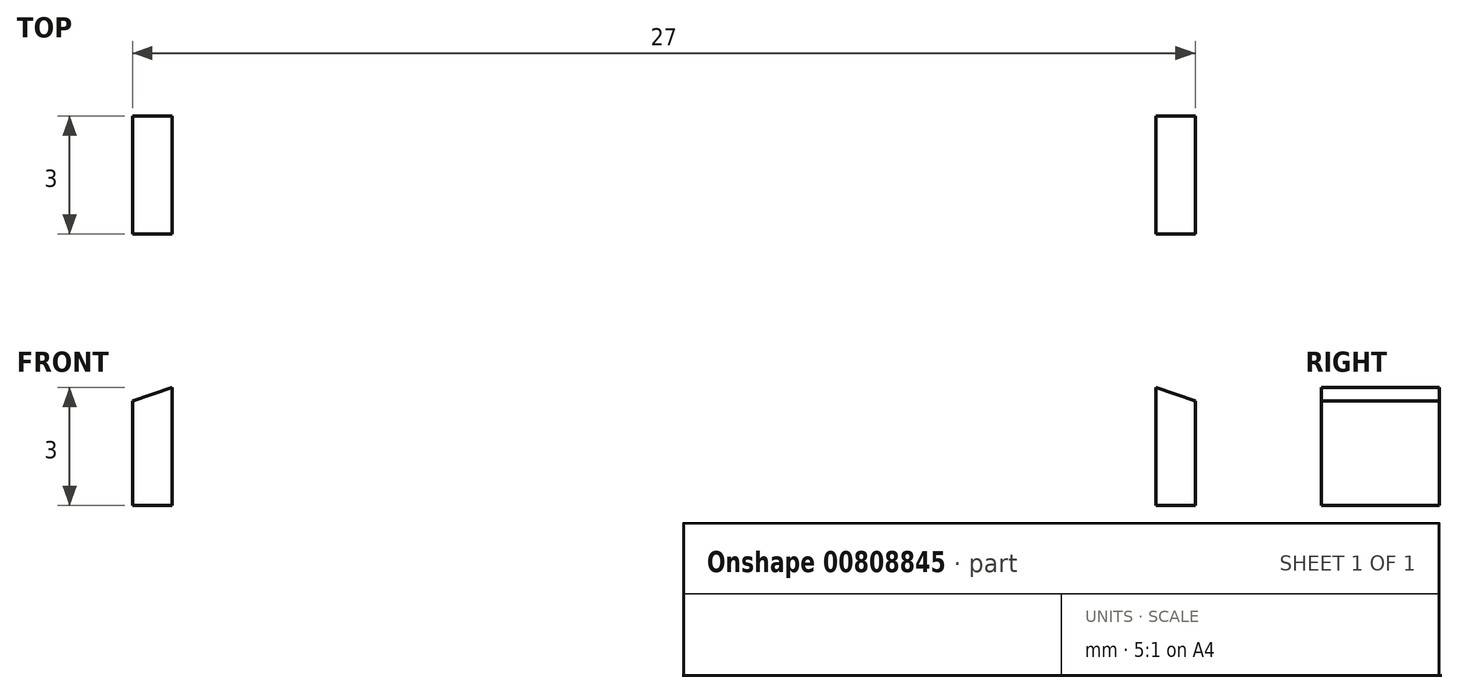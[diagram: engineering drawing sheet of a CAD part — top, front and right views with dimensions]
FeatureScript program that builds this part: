
annotation { "Feature Type Name" : "Feature", "Feature Type Description" : "" }
export const myFeature = defineFeature(function(context is Context, id is Id, definition is map)
    precondition{}
    {
        {
            var Q0;
            Q0=qCreatedBy(makeId("Front.planeOp"),FACE);
            var sketch = newSketch(context, id + "F0", { "sketchPlane" : qUnion([Q0])});
            skLineSegment(sketch, "E0.bottom", {"start": v(-35.5, 39) * mm, "end": v(35.5, 39) * mm});
            skLineSegment(sketch, "E0.top", {"start": v(-35.5, -39) * mm, "end": v(35.5, -39) * mm});
            skLineSegment(sketch, "E0.left", {"start": v(-35.5, 39) * mm, "end": v(-35.5, -39) * mm});
            skLineSegment(sketch, "E0.right", {"start": v(35.5, 39) * mm, "end": v(35.5, -39) * mm});
            skPoint(sketch, "E0.middle", {"position": v(0, 0) * mm});
            skLineSegment(sketch, "E1.top", {"start": v(-35.5, 31) * mm, "end": v(35.5, 31) * mm});
            skLineSegment(sketch, "E1.left", {"start": v(-35.5, -39) * mm, "end": v(-35.5, 31) * mm});
            skLineSegment(sketch, "E1.right", {"start": v(35.5, -39) * mm, "end": v(35.5, 31) * mm});
            skLineSegment(sketch, "E2.bottom", {"start": v(-12.5, 39) * mm, "end": v(12.5, 39) * mm});
            skLineSegment(sketch, "E2.top", {"start": v(-12.5, 31) * mm, "end": v(12.5, 31) * mm});
            skLineSegment(sketch, "E2.left", {"start": v(-12.5, 39) * mm, "end": v(-12.5, 31) * mm});
            skLineSegment(sketch, "E2.right", {"start": v(12.5, 39) * mm, "end": v(12.5, 31) * mm});
            skLineSegment(sketch, "E3", {"start": v(-35.5, 31) * mm, "end": v(-12.5, 39) * mm});
            skLineSegment(sketch, "E4", {"start": v(12.5, 39) * mm, "end": v(35.5, 31) * mm});
            skLineSegment(sketch, "E5.bottom", {"start": v(-32.5, -10) * mm, "end": v(-38.5, -10) * mm});
            skLineSegment(sketch, "E5.top", {"start": v(-32.5, 10) * mm, "end": v(-38.5, 10) * mm});
            skLineSegment(sketch, "E5.left", {"start": v(-32.5, -10) * mm, "end": v(-32.5, 10) * mm});
            skLineSegment(sketch, "E5.right", {"start": v(-38.5, -10) * mm, "end": v(-38.5, 10) * mm});
            skPoint(sketch, "E5.middle", {"position": v(-35.5, 0) * mm});
            skLineSegment(sketch, "E6.bottom", {"start": v(32.5, -10) * mm, "end": v(38.5, -10) * mm});
            skLineSegment(sketch, "E6.top", {"start": v(32.5, 10) * mm, "end": v(38.5, 10) * mm});
            skLineSegment(sketch, "E6.left", {"start": v(32.5, -10) * mm, "end": v(32.5, 10) * mm});
            skLineSegment(sketch, "E6.right", {"start": v(38.5, -10) * mm, "end": v(38.5, 10) * mm});
            skPoint(sketch, "E6.middle", {"position": v(35.5, 0) * mm});
            skLineSegment(sketch, "E7.bottom", {"start": v(-10, -42) * mm, "end": v(10, -42) * mm});
            skLineSegment(sketch, "E7.top", {"start": v(-10, -36) * mm, "end": v(10, -36) * mm});
            skLineSegment(sketch, "E7.left", {"start": v(-10, -42) * mm, "end": v(-10, -36) * mm});
            skLineSegment(sketch, "E7.right", {"start": v(10, -42) * mm, "end": v(10, -36) * mm});
            skPoint(sketch, "E7.middle", {"position": v(0, -39) * mm});
            skLineSegment(sketch, "E8.bottom", {"start": v(-12.5, 39) * mm, "end": v(-13.5, 39) * mm});
            skLineSegment(sketch, "E8.top", {"start": v(-12.5, 36) * mm, "end": v(-13.5, 36) * mm});
            skLineSegment(sketch, "E8.left", {"start": v(-12.5, 39) * mm, "end": v(-12.5, 36) * mm});
            skLineSegment(sketch, "E8.right", {"start": v(-13.5, 39) * mm, "end": v(-13.5, 36) * mm});
            skLineSegment(sketch, "E9.bottom", {"start": v(12.5, 39) * mm, "end": v(13.5, 39) * mm});
            skLineSegment(sketch, "E9.top", {"start": v(12.5, 36) * mm, "end": v(13.5, 36) * mm});
            skLineSegment(sketch, "E9.left", {"start": v(12.5, 39) * mm, "end": v(12.5, 36) * mm});
            skLineSegment(sketch, "E9.right", {"start": v(13.5, 39) * mm, "end": v(13.5, 36) * mm});
            skSolve(sketch);
        }
        {
            var Q0;
            {var subQ0=sQuery(id+"F0.wireOp",EDGE,"E2.top");Q0=makeQuery(id+"F0.imprint","IMPRINT",FACE,{"disambiguationData":[TD([[makeQuery(id+"F0.imprint","IMPRINT",EDGE,{"derivedFrom":subQ0}),-1.0]])]});}
            var Q1;
            {var subQ6=sQuery(id+"F0.wireOp",EDGE,"E2.left");Q1=makeQuery(id+"F0.imprint","IMPRINT",FACE,{"disambiguationData":[TD([[makeQuery(id+"F0.imprint","IMPRINT",EDGE,{"derivedFrom":subQ6}),-1.0]])]});}
            var Q2;
            {var subQ6=sQuery(id+"F0.wireOp",EDGE,"E2.right");Q2=makeQuery(id+"F0.imprint","IMPRINT",FACE,{"disambiguationData":[TD([[makeQuery(id+"F0.imprint","IMPRINT",EDGE,{"derivedFrom":subQ6}),1.0]])]});}
            extrude(context, id + "F1", {"entities" : qUnion([Q0, Q1, Q2]), "depth" : 3 * mm, "offsetDistance" : 25 * mm});
        }
        {
            var Q0;
            Q0=makeQuery(id+"F1.opExtrude","CAP_FACE",FACE,{"disambiguationData":[OSD([sQuery(id+"F0.wireOp",EDGE,"E0.top"),sQuery(id+"F0.wireOp",EDGE,"E1.left"),sQuery(id+"F0.wireOp",EDGE,"E1.right"),sQuery(id+"F0.wireOp",EDGE,"E2.top"),sQuery(id+"F0.wireOp",EDGE,"E2.left"),sQuery(id+"F0.wireOp",EDGE,"E2.right"),sQuery(id+"F0.wireOp",EDGE,"E3"),sQuery(id+"F0.wireOp",EDGE,"E4"),sQuery(id+"F0.wireOp",EDGE,"E5.bottom"),sQuery(id+"F0.wireOp",EDGE,"E5.top"),sQuery(id+"F0.wireOp",EDGE,"E5.left"),sQuery(id+"F0.wireOp",EDGE,"E6.bottom"),sQuery(id+"F0.wireOp",EDGE,"E6.top"),sQuery(id+"F0.wireOp",EDGE,"E6.left"),sQuery(id+"F0.wireOp",EDGE,"E7.top"),sQuery(id+"F0.wireOp",EDGE,"E7.left"),sQuery(id+"F0.wireOp",EDGE,"E7.right"),sQuery(id+"F0.wireOp",EDGE,"E8.top"),sQuery(id+"F0.wireOp",EDGE,"E8.right"),sQuery(id+"F0.wireOp",EDGE,"E9.top"),sQuery(id+"F0.wireOp",EDGE,"E9.right")])],"isStart":false});
            var sketch = newSketch(context, id + "F2", { "sketchPlane" : qUnion([Q0])});
            skLineSegment(sketch, "E10.bottom", {"start": v(22.5, 31) * mm, "end": v(-32.5, 31) * mm});
            skLineSegment(sketch, "E10.top", {"start": v(22.5, -36) * mm, "end": v(-32.5, -36) * mm});
            skLineSegment(sketch, "E10.left", {"start": v(22.5, 31) * mm, "end": v(22.5, -36) * mm});
            skLineSegment(sketch, "E10.right", {"start": v(-32.5, 31) * mm, "end": v(-32.5, -36) * mm});
            skPoint(sketch, "E10.middle", {"position": v(-5, -2.5) * mm});
            skLineSegment(sketch, "E11.bottom", {"start": v(22.5, 31) * mm, "end": v(32.5, 31) * mm});
            skLineSegment(sketch, "E11.top", {"start": v(22.5, -36) * mm, "end": v(32.5, -36) * mm});
            skLineSegment(sketch, "E11.right", {"start": v(32.5, 31) * mm, "end": v(32.5, -36) * mm});
            skCircle(sketch, "E12", {"center": v(27.5, -16) * mm, "radius": 5 * mm});
            skCircle(sketch, "E13", {"center": v(27.5, -16) * mm, "radius": 2.6 * mm});
            skSolve(sketch);
        }
        {
            var Q0;
            Q0=makeQuery(id+"F2.imprint","IMPRINT",FACE,{"disambiguationData":[TD([[makeQuery(id+"F2.imprint","IMPRINT",EDGE,{"derivedFrom":sQuery(id+"F2.wireOp",EDGE,"E13")}),1.0]])]});
            extrude(context, id + "F3", {"entities" : qUnion([Q0]), "operationType" : NewBodyOperationType.REMOVE, "oppositeDirection" : true, "depth" : 25 * mm, "offsetDistance" : 25 * mm});
        }
    });
